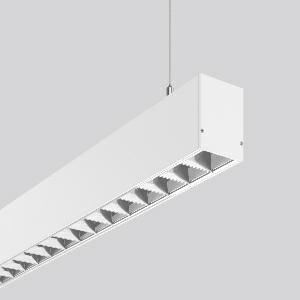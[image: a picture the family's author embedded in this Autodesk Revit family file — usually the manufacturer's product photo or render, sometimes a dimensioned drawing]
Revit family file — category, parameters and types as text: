
# Revit family: less_is_more_50_312342_002_a139
name_source: partatom
category: Lighting Fixtures
units: mm (PartAtom-declared; Revit-internal decimal feet)

## family parameters
Cut with Voids When Loaded = No
Host = Face
Light Source = No
Part Type = Normal
Room Calculation Point = No
Round Connector Dimension = Use Diameter
Shared = No

## types (1)
- LESS IS MORE 50 (1 x LED Modul 830, 4800 lm, 3000)
    Apparent Load = 46 VA
    CIE Flux Codes = 95 100 100 63 100
    Color Rendering = 80
    Color Temperature = 3000
    Default Elevation = 1800 mm
    Description = Series: LESS IS MORE 50
Linear pendant luminaire for aesthetically sophisticated lighting. Housing: extruded aluminium profile, powder-coated. End cap aluminium powder-coated. Canopy made of aluminium, powder-coated. Alea optical system: Reflector structure (ABS, Aluminium-coated, highly polished) with integrated diffuser made of non-yellowing plastic (PMMA) opal for glare-free light at the workstation (screen-compliant according to EN 12464-1). Direct 65%, indirect 35% light emission. Suitable for pendant. 2-point steel cable suspension freely positionable and infinitely height-adjustable. Special lengths available on request. LED unit with integrated converter interchangeable and removable. Suitable for through-wiring. With sensors or as a safety luminaire on request. 
Colour: traffic white, matt (RAL 9016)
Length: 1127 mm
Width: 57 mm
Height: 75 mm
Suspension length: 2000 mm
Lamp: LED
Socket: without socket
Colour temperature: 3000K
Colour rendering index (CRI): 80
Light source: LED
Socket lamp2: Without base
Colour temperature: 3000K
System power: 46 W
Rated luminous flux: 4800 lm
Luminous efficiency: 104 lm/W
Control gear: Regulated power supply
Control gear: Regulated power supply
Protection class: I
Type of protection: IP 20
    Height = 75 mm
    Lamp = 1 x LED Modul 830
    Lamp Light Flux = 4800 lm
    Lamp count = 1
    Length = 1127 mm
    Lifetime = 50000 h
    Luminous efficacy = 104 lm/W
    Manufacturer = RZB
    ModVariant = No
    Model = 312342.002
    Mounting Place = Ceiling
    Mounting Type = Pendant
    Number of Poles = 1
    OnlyDefault = Yes
    Power Factor = 1
    Product Name = LESS IS MORE 50
    Product group = Pendant LED linear luminaires
    ProductGroupID = 907
    Protection Class = Protection class I
    Protection Degree = IP 20
    RLX_Detail_Level = 1
    RLX_Emergency_Light_Flux = 0 lm
    RLX_Emergency_Type = 0
    RLX_Emergency_Type_DB = No
    RlxData = <blob elided: 37417 chars, md5=0cea5efa>
    Socket = socket
    Standby Power = 0 W
    System Light Flux = 4800 lm
    System Power = 46 W
    Type Comments = Product without accessories
    Type Image = 312342.002.jpg
    URL = http://relux.com
    VarID = ---
    Voltage = 230 V
    Voltage Range = 220-240 V
    Weight = 0.00 kg
    Width = 57 mm

## geometry (parser evidence)
native form markers: Blend x4, Sweep x13
no freeform markers — native parametric forms only
